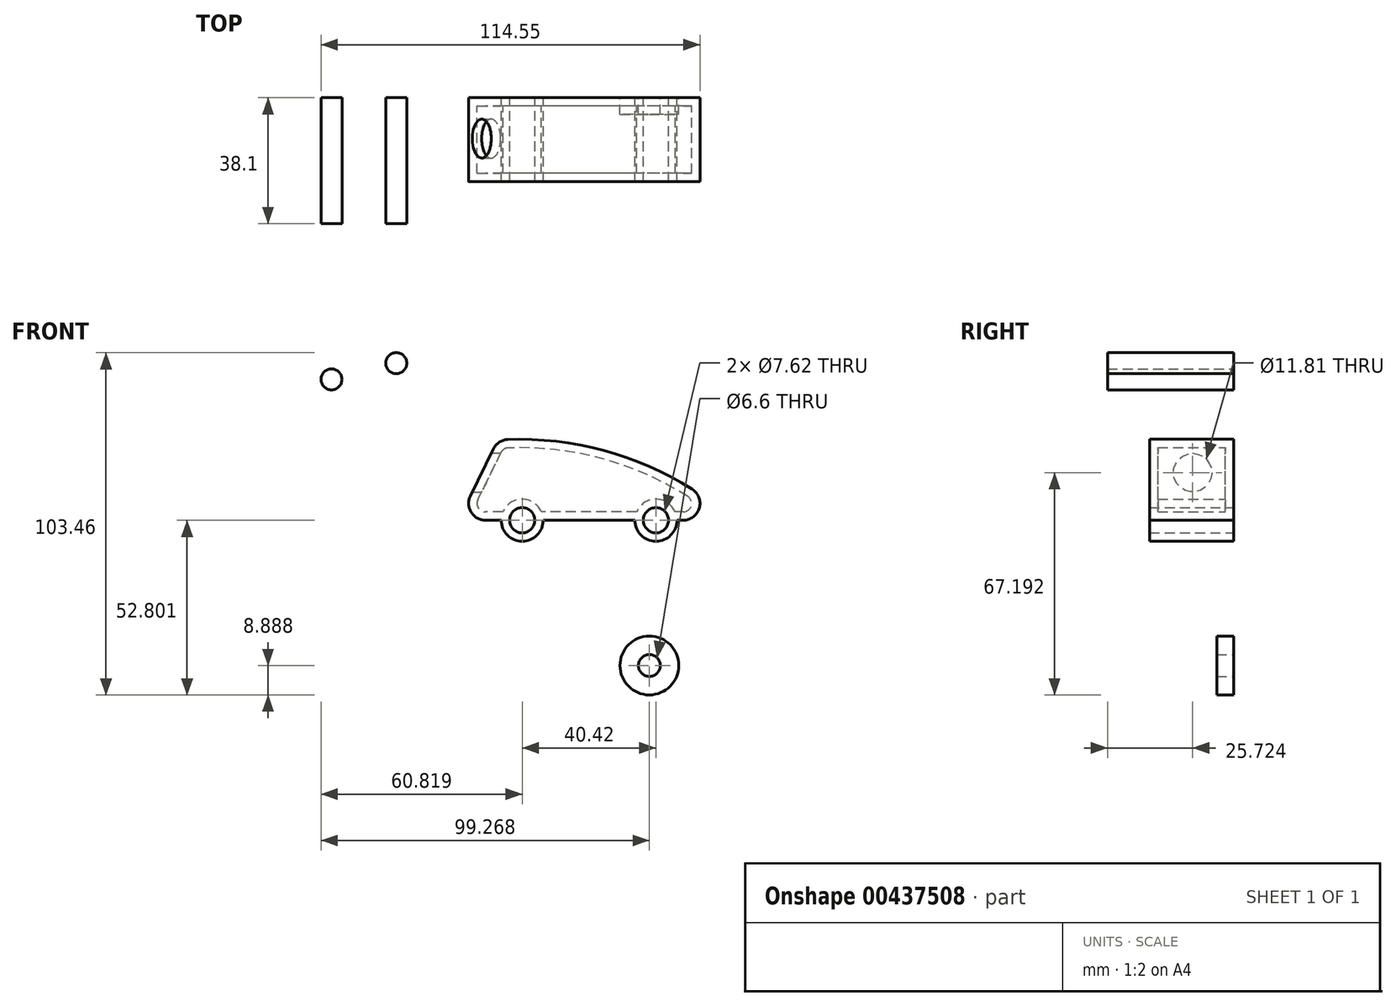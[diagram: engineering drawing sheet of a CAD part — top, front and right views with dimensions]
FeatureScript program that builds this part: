
annotation { "Feature Type Name" : "Feature", "Feature Type Description" : "" }
export const myFeature = defineFeature(function(context is Context, id is Id, definition is map)
    precondition{}
    {
        {
            var Q0;
            Q0=qCreatedBy(makeId("Front.planeOp"),FACE);
            var sketch = newSketch(context, id + "F0", { "sketchPlane" : qUnion([Q0])});
            skArc(sketch, "E0", {"start": v(43.4, 22.33) * mm, "mid": v(16.68, 34.06) * mm, "end": v(-12.32, 37.36) * mm});
            skLineSegment(sketch, "E1", {"start": v(40.68, 12.95) * mm, "end": v(-19.08, 12.95) * mm});
            skLineSegment(sketch, "E2", {"start": v(-23.64, 20.26) * mm, "end": v(-16.7, 34.51) * mm});
            skCircle(sketch, "E3", {"center": v(32.45, 12.95) * mm, "radius": 6.35 * mm});
            skCircle(sketch, "E4", {"center": v(-7.97, 12.95) * mm, "radius": 6.35 * mm});
            skCircle(sketch, "E5", {"center": v(32.45, 12.95) * mm, "radius": 3.81 * mm});
            skCircle(sketch, "E6", {"center": v(-7.97, 12.95) * mm, "radius": 3.81 * mm});
            skPoint(sketch, "E7.visualSharp", {"position": v(55.89, 12.95) * mm});
            skArc(sketch, "E7.filletArc", {"start": v(40.68, 12.95) * mm, "mid": v(45.56, 16.62) * mm, "end": v(43.4, 22.33) * mm});
            skPoint(sketch, "E8.visualSharp", {"position": v(-15.39, 37.2) * mm});
            skArc(sketch, "E8.filletArc", {"start": v(-12.32, 37.36) * mm, "mid": v(-14.9, 36.55) * mm, "end": v(-16.7, 34.51) * mm});
            skPoint(sketch, "E9.visualSharp", {"position": v(-27.2, 12.95) * mm});
            skArc(sketch, "E9.filletArc", {"start": v(-23.64, 20.26) * mm, "mid": v(-23.38, 15.34) * mm, "end": v(-19.08, 12.95) * mm});
            skSolve(sketch);
        }
        {
            var Q0;
            Q0 = qSketchRegion(id + "F0", true);
            extrude(context, id + "F1", {"entities" : qUnion([Q0]), "depth" : 25.4 * mm});
        }
        {
            var Q0;
            Q0=makeQuery(id+"F1.opExtrude","CAP_FACE",FACE,{"disambiguationData":[OSD([sQuery(id+"F0.wireOp",EDGE,"E0"),sQuery(id+"F0.wireOp",EDGE,"E1"),sQuery(id+"F0.wireOp",EDGE,"E2")])],"isStart":true});
            var Q1;
            Q1=makeQuery(id+"F1.opExtrude","SWEPT_BODY",BODY,{"disambiguationData":[OSD([sQuery(id+"F0.wireOp",EDGE,"E0"),sQuery(id+"F0.wireOp",EDGE,"E1"),sQuery(id+"F0.wireOp",EDGE,"E2")])]});
            shell(context, id + "F2", {"isHollow" : true, "entities" : qUnion([Q0]), "parts" : qUnion([Q1]), "thickness" : 2.54 * mm});
        }
        {
            var Q0;
            Q0=qCreatedBy(makeId("Front.planeOp"),FACE);
            var sketch = newSketch(context, id + "F3", { "sketchPlane" : qUnion([Q0])});
            skCircle(sketch, "E10", {"center": v(-40.87, -40) * mm, "radius": 12.57 * mm});
            skSolve(sketch);
        }
        {
            var Q0;
            Q0 = qSketchRegion(id + "F3", true);
            extrude(context, id + "F4", {"entities" : qUnion([Q0]), "depth" : 25.4 * mm});
        }
        {
            var Q0;
            Q0=qCreatedBy(makeId("Front.planeOp"),FACE);
            var sketch = newSketch(context, id + "F5", { "sketchPlane" : qUnion([Q0])});
            skCircle(sketch, "E11", {"center": v(-65.62, 55.55) * mm, "radius": 3.18 * mm});
            skCircle(sketch, "E12", {"center": v(-46.05, 60.44) * mm, "radius": 3.18 * mm});
            skSolve(sketch);
        }
        {
            var Q0;
            Q0 = qSketchRegion(id + "F5", true);
            extrude(context, id + "F6", {"entities" : qUnion([Q0]), "depth" : 38.1 * mm});
        }
        {
            var Q0;
            Q0=makeQuery(id+"F4.opExtrude","SWEPT_BODY",BODY,{"disambiguationData":[OSD([sQuery(id+"F3.wireOp",EDGE,"E10")])]});
            deleteBodies(context, id + "F7", {"entities" : qUnion([Q0])});
        }
        {
            var Q0;
            Q0=qCreatedBy(makeId("Front.planeOp"),FACE);
            var sketch = newSketch(context, id + "F8", { "sketchPlane" : qUnion([Q0])});
            skCircle(sketch, "E13", {"center": v(30.48, -30.96) * mm, "radius": 8.9 * mm});
            skCircle(sketch, "E14", {"center": v(30.48, -30.96) * mm, "radius": 3.3 * mm});
            skSolve(sketch);
        }
        {
            var Q0;
            Q0 = qSketchRegion(id + "F8", true);
            extrude(context, id + "F9", {"entities" : qUnion([Q0]), "depth" : 5.08 * mm});
        }
        {
            var Q0;
            Q0=qCreatedBy(makeId("Right.planeOp"),FACE);
            var sketch = newSketch(context, id + "F10", { "sketchPlane" : qUnion([Q0])});
            skCircle(sketch, "E15", {"center": v(-12.38, 27.34) * mm, "radius": 5.9 * mm});
            skSolve(sketch);
        }
        {
            var Q0;
            Q0 = qSketchRegion(id + "F10", true);
            extrude(context, id + "F11", {"entities" : qUnion([Q0]), "operationType" : NewBodyOperationType.REMOVE, "oppositeDirection" : true, "depth" : 29.46 * mm});
        }
    });
